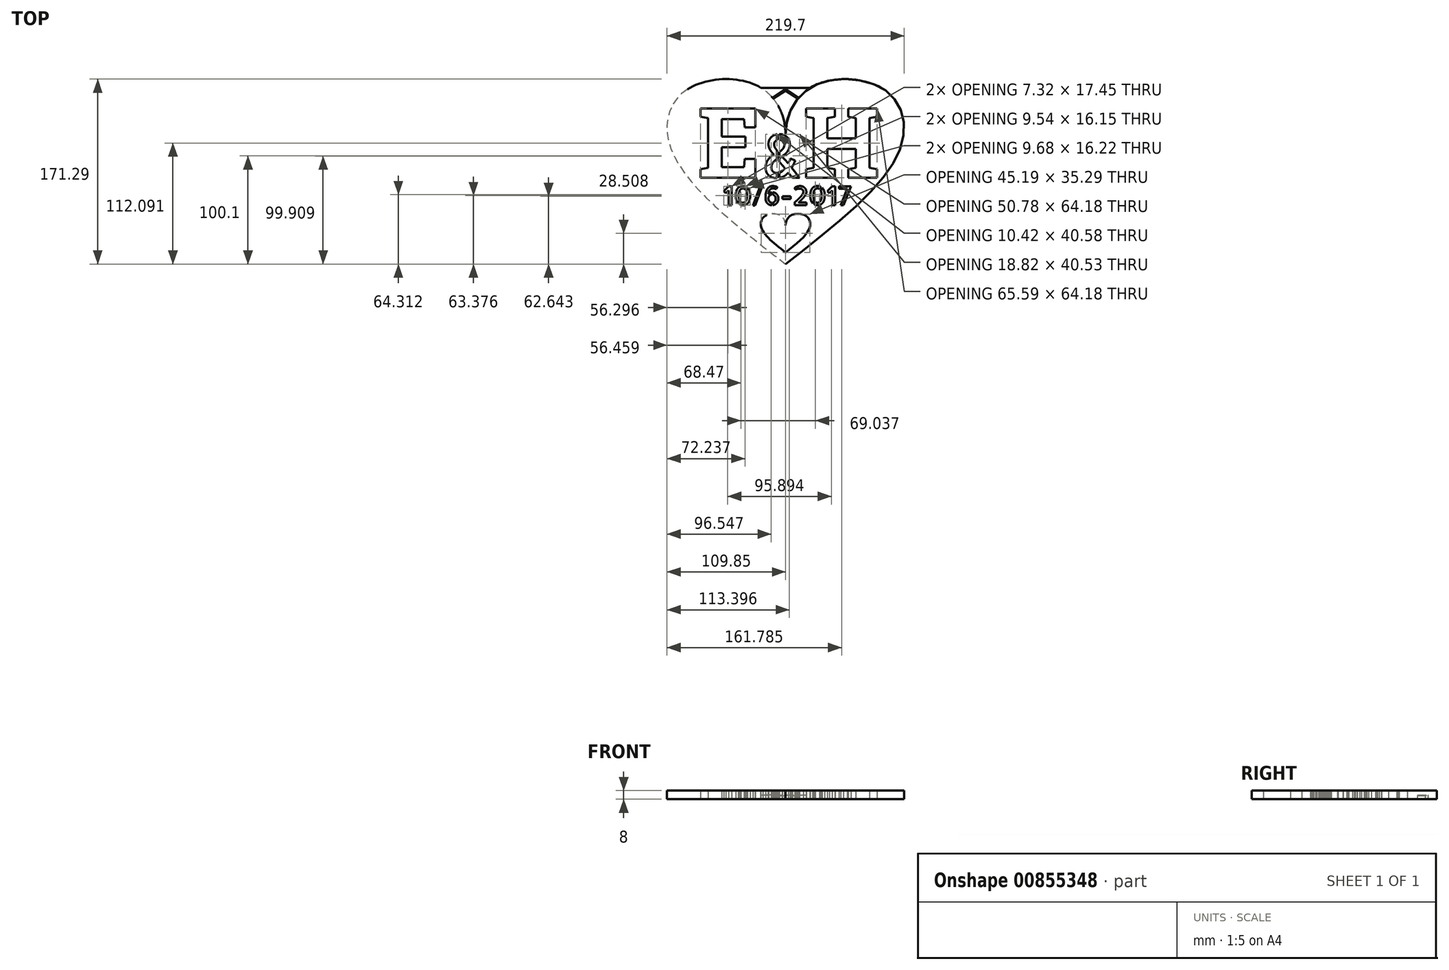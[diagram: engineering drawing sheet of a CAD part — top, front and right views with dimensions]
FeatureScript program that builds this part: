
annotation { "Feature Type Name" : "Feature", "Feature Type Description" : "" }
export const myFeature = defineFeature(function(context is Context, id is Id, definition is map)
    precondition{}
    {
        {
            var Q0;
            Q0=qCreatedBy(makeId("Top.planeOp"),FACE);
            var sketch = newSketch(context, id + "F0", { "sketchPlane" : qUnion([Q0])});
            skFitSpline(sketch, "E0", {"points": [v(0, 0) * mm, v(-26.1, 45.02) * mm, v(-93.72, 39.88) * mm, v(-106.22, -13.05) * mm, v(0, -120) * mm], "startDerivative": vector(0, 265.57) * mm, "endDerivative": vector(395.16, -307.05) * mm});
            skLineSegment(sketch, "E1", {"start": v(0, -120) * mm, "end": v(0, 0) * mm});
            skFitSpline(sketch, "E2.MirrorCS", {"points": [v(0, 0) * mm, v(26.1, 45.02) * mm, v(93.72, 39.88) * mm, v(106.22, -13.05) * mm, v(0, -120) * mm], "startDerivative": vector(0, 265.57) * mm, "endDerivative": vector(-395.16, -307.05) * mm});
            skSolve(sketch);
        }
        {
            var Q0;
            {var subQ0=sQuery(id+"F0.wireOp",EDGE,"E0");Q0=makeQuery(id+"F0.imprint","IMPRINT",FACE,{"disambiguationData":[TD([[makeQuery(id+"F0.imprint","IMPRINT",EDGE,{"derivedFrom":subQ0}),1.0]])]});}
            var sketch = newSketch(context, id + "F1", { "sketchPlane" : qUnion([Q0])});
            skText(sketch, "E3", { "text": "E", "fontName": "RobotoSlab-Bold.ttf"});
            skText(sketch, "E4", { "text": "H", "fontName": "RobotoSlab-Bold.ttf"});
            skText(sketch, "E5", { "text": "&", "fontName": "AllertaStencil-Regular.ttf"});
            skText(sketch, "E6", { "text": "10/6-2017", "fontName": "AllertaStencil-Regular.ttf"});
            const initialGuessF1  = {"E3": [-0.08125, -0.04, 1, 0, 0.065], "E4": [0.01667, -0.04, 1, 0, 0.065], "E5": [-0.02247, -0.04, 1, 0, 0.04], "E6": [-0.0579, -0.06535, 1, 0, 0.01746]};
            skSetInitialGuess(sketch, initialGuessF1);
            skSolve(sketch);
        }
        {
            var Q0;
            {var subQ0=sQuery(id+"F0.wireOp",EDGE,"E0");Q0=makeQuery(id+"F0.imprint","IMPRINT",FACE,{"disambiguationData":[TD([[makeQuery(id+"F0.imprint","IMPRINT",EDGE,{"derivedFrom":subQ0}),1.0]])]});}
            var Q1;
            {var subQ0=sQuery(id+"F0.wireOp",EDGE,"E1");Q1=makeQuery(id+"F0.imprint","IMPRINT",FACE,{"disambiguationData":[TD([[makeQuery(id+"F0.imprint","IMPRINT",EDGE,{"derivedFrom":subQ0}),-1.0]])]});}
            extrude(context, id + "F2", {"entities" : qUnion([Q0, Q1]), "depth" : 8 * mm, "offsetDistance" : 25 * mm});
        }
        {
            var Q0;
            Q0 = qSketchRegion(id + "F1", true);
            extrude(context, id + "F3", {"entities" : qUnion([Q0]), "operationType" : NewBodyOperationType.REMOVE, "depth" : 25 * mm, "offsetDistance" : 25 * mm});
        }
        {
            var Q0;
            Q0=qCreatedBy(makeId("Top.planeOp"),FACE);
            var sketch = newSketch(context, id + "F4", { "sketchPlane" : qUnion([Q0])});
            skLineSegment(sketch, "E7", {"start": v(0, 0) * mm, "end": v(0, 120.65) * mm, "construction": true});
            skLineSegment(sketch, "E8.bottom", {"start": v(-22.8, 43.18) * mm, "end": v(22.8, 43.18) * mm});
            skLineSegment(sketch, "E8.top", {"start": v(-22.8, 33.18) * mm, "end": v(-11.4, 33.18) * mm});
            skLineSegment(sketch, "E8.left", {"start": v(-22.8, 43.18) * mm, "end": v(-22.8, 33.18) * mm});
            skLineSegment(sketch, "E8.right", {"start": v(22.8, 43.18) * mm, "end": v(22.8, 33.18) * mm});
            skLineSegment(sketch, "E9", {"start": v(-11.4, 33.18) * mm, "end": v(0, 40.57) * mm});
            skLineSegment(sketch, "E10", {"start": v(0, 40.57) * mm, "end": v(11.4, 33.18) * mm});
            skLineSegment(sketch, "E11.trimOffspring", {"start": v(11.4, 33.18) * mm, "end": v(22.8, 33.18) * mm});
            skSolve(sketch);
        }
        {
            var Q0;
            Q0=makeQuery(id+"F4.imprint","IMPRINT",FACE,{"disambiguationData":[TD([[makeQuery(id+"F4.imprint","IMPRINT",EDGE,{"derivedFrom":sQuery(id+"F4.wireOp",EDGE,"E8.bottom")}),-1.0]])]});
            extrude(context, id + "F5", {"entities" : qUnion([Q0]), "operationType" : NewBodyOperationType.ADD, "depth" : 4 * mm, "offsetDistance" : 25 * mm});
        }
        {
            var Q0;
            Q0=makeQuery(id+"F5.opExtrude","CAP_EDGE",EDGE,{"disambiguationData":[OSD([sQuery(id+"F4.wireOp",EDGE,"E9")])],"isStart":false});
            var Q1;
            Q1=makeQuery(id+"F5.opExtrude","CAP_EDGE",EDGE,{"disambiguationData":[OSD([sQuery(id+"F4.wireOp",EDGE,"E10")])],"isStart":false});
            chamfer(context, id + "F6", {"entities" : qUnion([Q0, Q1]), "width" : 1 * mm, "tangentPropagation" : true});
        }
        {
            var Q0;
            Q0=qCreatedBy(makeId("Top.planeOp"),FACE);
            var sketch = newSketch(context, id + "F7", { "sketchPlane" : qUnion([Q0])});
            skFitSpline(sketch, "E12", {"points": [v(0, -84.14) * mm, v(-5.44, -74.76) * mm, v(-19.53, -75.83) * mm, v(-22.13, -86.86) * mm, v(0, -109.14) * mm], "startDerivative": vector(0, 55.33) * mm, "endDerivative": vector(82.32, -63.97) * mm});
            skLineSegment(sketch, "E13", {"start": v(0, 5.51) * mm, "end": v(0, 30.51) * mm});
            skFitSpline(sketch, "E14.MirrorCS", {"points": [v(0, -84.14) * mm, v(5.44, -74.76) * mm, v(19.53, -75.83) * mm, v(22.13, -86.86) * mm, v(0, -109.14) * mm], "startDerivative": vector(0, 55.33) * mm, "endDerivative": vector(-82.32, -63.97) * mm});
            skSolve(sketch);
        }
        {
            var Q0;
            Q0 = qSketchRegion(id + "F7", true);
            extrude(context, id + "F8", {"entities" : qUnion([Q0]), "operationType" : NewBodyOperationType.REMOVE, "depth" : 25 * mm, "offsetDistance" : 25 * mm});
        }
    });
